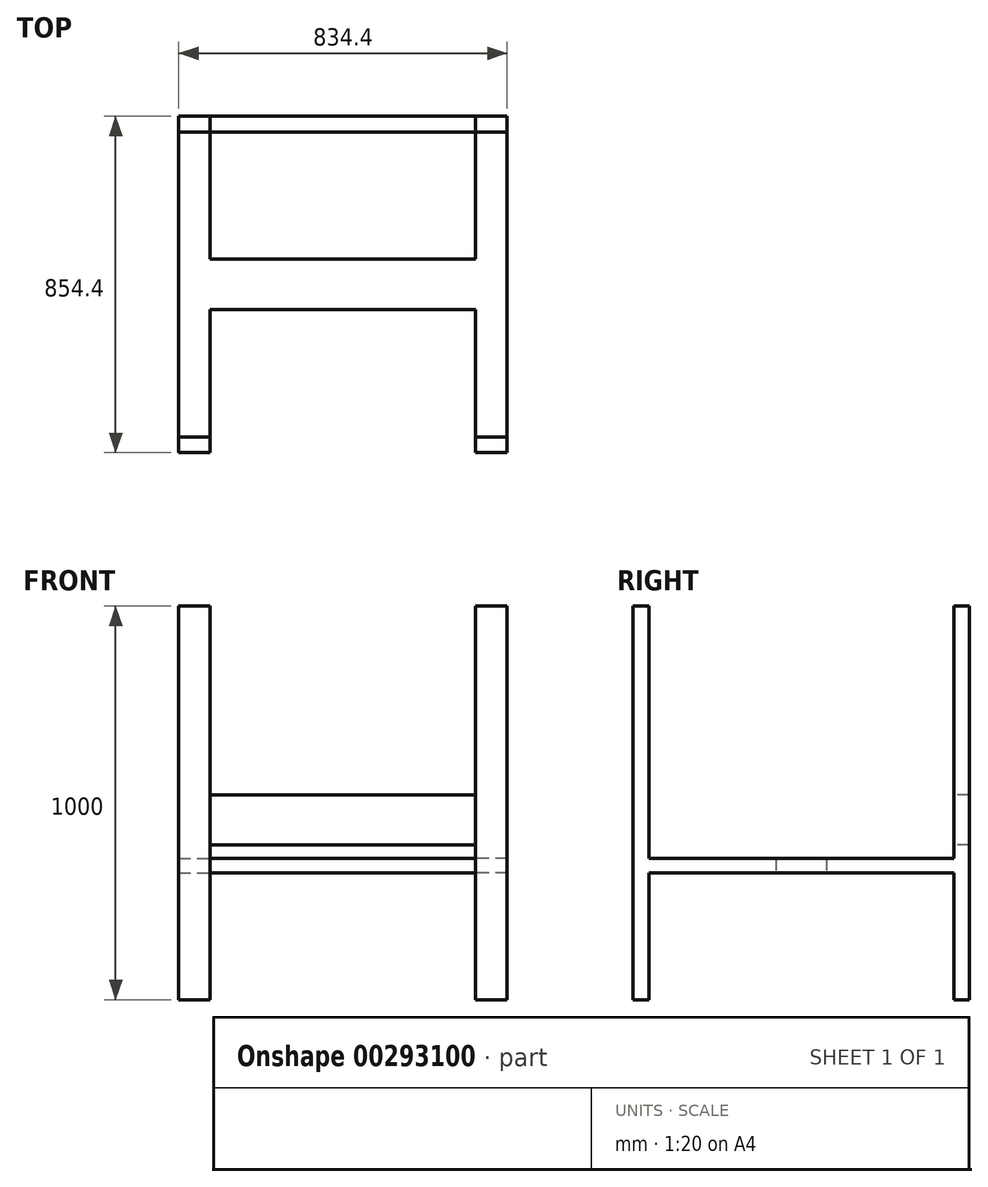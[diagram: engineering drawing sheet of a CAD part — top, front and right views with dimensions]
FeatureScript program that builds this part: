
annotation { "Feature Type Name" : "Feature", "Feature Type Description" : "" }
export const myFeature = defineFeature(function(context is Context, id is Id, definition is map)
    precondition{}
    {
        {
            var Q0;
            Q0=qCreatedBy(makeId("Top.planeOp"),FACE);
            var sketch = newSketch(context, id + "F0", { "sketchPlane" : qUnion([Q0])});
            skLineSegment(sketch, "E0.bottom", {"start": v(-457.2, 457.2) * mm, "end": v(457.2, 457.2) * mm});
            skLineSegment(sketch, "E0.top", {"start": v(-457.2, -457.2) * mm, "end": v(457.2, -457.2) * mm});
            skLineSegment(sketch, "E0.left", {"start": v(-457.2, 457.2) * mm, "end": v(-457.2, -457.2) * mm});
            skLineSegment(sketch, "E0.right", {"start": v(457.2, 457.2) * mm, "end": v(457.2, -457.2) * mm});
            skPoint(sketch, "E0.middle", {"position": v(0, 0) * mm});
            skLineSegment(sketch, "E1.bottom", {"start": v(-417.2, -427.2) * mm, "end": v(-337.2, -427.2) * mm});
            skLineSegment(sketch, "E1.top", {"start": v(-417.2, -387.2) * mm, "end": v(-337.2, -387.2) * mm});
            skLineSegment(sketch, "E1.left", {"start": v(-417.2, -427.2) * mm, "end": v(-417.2, -387.2) * mm});
            skLineSegment(sketch, "E1.right", {"start": v(-337.2, -427.2) * mm, "end": v(-337.2, -387.2) * mm});
            skLineSegment(sketch, "E2.MirrorCS", {"start": v(-417.2, 387.2) * mm, "end": v(-337.2, 387.2) * mm});
            skLineSegment(sketch, "E3.MirrorCS", {"start": v(-417.2, 427.2) * mm, "end": v(-337.2, 427.2) * mm});
            skLineSegment(sketch, "E4.MirrorCS", {"start": v(-337.2, 427.2) * mm, "end": v(-337.2, 387.2) * mm});
            skLineSegment(sketch, "E5.MirrorCS", {"start": v(-417.2, 427.2) * mm, "end": v(-417.2, 387.2) * mm});
            skLineSegment(sketch, "E6.MirrorCS", {"start": v(337.2, 427.2) * mm, "end": v(337.2, 387.2) * mm});
            skLineSegment(sketch, "E7.MirrorCS", {"start": v(417.2, 387.2) * mm, "end": v(337.2, 387.2) * mm});
            skLineSegment(sketch, "E8.MirrorCS", {"start": v(417.2, 427.2) * mm, "end": v(337.2, 427.2) * mm});
            skLineSegment(sketch, "E9.MirrorCS", {"start": v(417.2, 427.2) * mm, "end": v(417.2, 387.2) * mm});
            skLineSegment(sketch, "E10.MirrorCS", {"start": v(337.2, -427.2) * mm, "end": v(337.2, -387.2) * mm});
            skLineSegment(sketch, "E11.MirrorCS", {"start": v(417.2, -387.2) * mm, "end": v(337.2, -387.2) * mm});
            skLineSegment(sketch, "E12.MirrorCS", {"start": v(417.2, -427.2) * mm, "end": v(337.2, -427.2) * mm});
            skLineSegment(sketch, "E13.MirrorCS", {"start": v(417.2, -427.2) * mm, "end": v(417.2, -387.2) * mm});
            skSolve(sketch);
        }
        {
            var Q0;
            Q0=makeQuery(id+"F0.imprint","IMPRINT",FACE,{"disambiguationData":[TD([[makeQuery(id+"F0.imprint","IMPRINT",EDGE,{"derivedFrom":sQuery(id+"F0.wireOp",EDGE,"E0.bottom")}),-1.0]])]});
            var Q1;
            Q1=makeQuery(id+"F0.imprint","IMPRINT",FACE,{"disambiguationData":[TD([[makeQuery(id+"F0.imprint","IMPRINT",EDGE,{"derivedFrom":sQuery(id+"F0.wireOp",EDGE,"E1.bottom")}),1.0]])]});
            var Q2;
            Q2=makeQuery(id+"F0.imprint","IMPRINT",FACE,{"disambiguationData":[TD([[makeQuery(id+"F0.imprint","IMPRINT",EDGE,{"derivedFrom":sQuery(id+"F0.wireOp",EDGE,"E6.MirrorCS")}),1.0]])]});
            var Q3;
            Q3=makeQuery(id+"F0.imprint","IMPRINT",FACE,{"disambiguationData":[TD([[makeQuery(id+"F0.imprint","IMPRINT",EDGE,{"derivedFrom":sQuery(id+"F0.wireOp",EDGE,"E10.MirrorCS")}),-1.0]])]});
            var Q4;
            Q4=makeQuery(id+"F0.imprint","IMPRINT",FACE,{"disambiguationData":[TD([[makeQuery(id+"F0.imprint","IMPRINT",EDGE,{"derivedFrom":sQuery(id+"F0.wireOp",EDGE,"E2.MirrorCS")}),1.0]])]});
            var Q5;
            Q5=makeQuery(id+"F0.imprint","IMPRINT",FACE,{"disambiguationData":[TD([[makeQuery(id+"F0.imprint","IMPRINT",EDGE,{"derivedFrom":sQuery(id+"F0.wireOp",EDGE,"8inZ48Au-BpXX-FDBc-ttF8-S0e7Y6VRDIfR.bottom")}),-1.0]])]});
            extrude(context, id + "F1", {"entities" : qUnion([Q0, Q1, Q2, Q3, Q4, Q5]), "depth" : 40 * mm});
        }
        {
            var Q0;
            Q0=makeQuery(id+"F0.imprint","IMPRINT",FACE,{"disambiguationData":[TD([[makeQuery(id+"F0.imprint","IMPRINT",EDGE,{"derivedFrom":sQuery(id+"F0.wireOp",EDGE,"E1.bottom")}),1.0]])]});
            var Q1;
            Q1=makeQuery(id+"F0.imprint","IMPRINT",FACE,{"disambiguationData":[TD([[makeQuery(id+"F0.imprint","IMPRINT",EDGE,{"derivedFrom":sQuery(id+"F0.wireOp",EDGE,"E2.MirrorCS")}),1.0]])]});
            var Q2;
            Q2=makeQuery(id+"F0.imprint","IMPRINT",FACE,{"disambiguationData":[TD([[makeQuery(id+"F0.imprint","IMPRINT",EDGE,{"derivedFrom":sQuery(id+"F0.wireOp",EDGE,"E10.MirrorCS")}),-1.0]])]});
            var Q3;
            Q3=makeQuery(id+"F0.imprint","IMPRINT",FACE,{"disambiguationData":[TD([[makeQuery(id+"F0.imprint","IMPRINT",EDGE,{"derivedFrom":sQuery(id+"F0.wireOp",EDGE,"E6.MirrorCS")}),1.0]])]});
            extrude(context, id + "F2", {"entities" : qUnion([Q0, Q1, Q2, Q3]), "operationType" : NewBodyOperationType.ADD, "oppositeDirection" : true, "depth" : 1000 * mm});
        }
        {
            var Q0;
            Q0=makeQuery(id+"F0.imprint","IMPRINT",FACE,{"disambiguationData":[TD([[makeQuery(id+"F0.imprint","IMPRINT",EDGE,{"derivedFrom":sQuery(id+"F0.wireOp",EDGE,"E0.bottom")}),-1.0]])]});
            cPlane(context, id + "F3", {"entities" : qUnion([Q0]), "cplaneType" : CPlaneType.OFFSET, "offset" : 607 * mm, "oppositeDirection" : true, "width" : 150 * mm, "height" : 150 * mm});
        }
        {
            var Q0;
            Q0=qCreatedBy(id+"F3.planeOp",FACE);
            var sketch = newSketch(context, id + "F4", { "sketchPlane" : qUnion([Q0])});
            skLineSegment(sketch, "E14.bottom", {"start": v(-337.2, 427.2) * mm, "end": v(337.2, 427.2) * mm});
            skLineSegment(sketch, "E14.top", {"start": v(-337.2, 387.2) * mm, "end": v(337.2, 387.2) * mm});
            skLineSegment(sketch, "E14.left", {"start": v(-337.2, 427.2) * mm, "end": v(-337.2, 387.2) * mm});
            skLineSegment(sketch, "E14.right", {"start": v(337.2, 427.2) * mm, "end": v(337.2, 387.2) * mm});
            skSolve(sketch);
        }
        {
            var Q0;
            Q0=makeQuery(id+"F4.imprint","IMPRINT",FACE,{"disambiguationData":[TD([[makeQuery(id+"F4.imprint","IMPRINT",EDGE,{"derivedFrom":sQuery(id+"F4.wireOp",EDGE,"E14.bottom")}),-1.0]])]});
            extrude(context, id + "F5", {"entities" : qUnion([Q0]), "operationType" : NewBodyOperationType.ADD, "depth" : 127 * mm});
        }
        {
            var Q0;
            Q0=makeQuery(id+"F0.imprint","IMPRINT",FACE,{"disambiguationData":[TD([[makeQuery(id+"F0.imprint","IMPRINT",EDGE,{"derivedFrom":sQuery(id+"F0.wireOp",EDGE,"E0.bottom")}),-1.0]])]});
            cPlane(context, id + "F6", {"entities" : qUnion([Q0]), "cplaneType" : CPlaneType.OFFSET, "offset" : 678 * mm, "oppositeDirection" : true, "width" : 150 * mm, "height" : 150 * mm});
        }
        {
            var Q0;
            Q0=qCreatedBy(id+"F6.planeOp",FACE);
            var sketch = newSketch(context, id + "F7", { "sketchPlane" : qUnion([Q0])});
            skLineSegment(sketch, "E15.bottom", {"start": v(-417.2, -387.2) * mm, "end": v(-337.2, -387.2) * mm});
            skLineSegment(sketch, "E15.top", {"start": v(-417.2, 387.2) * mm, "end": v(-337.2, 387.2) * mm});
            skLineSegment(sketch, "E15.left", {"start": v(-417.2, -387.2) * mm, "end": v(-417.2, 387.2) * mm});
            skLineSegment(sketch, "E15.right", {"start": v(-337.2, -387.2) * mm, "end": v(-337.2, 387.2) * mm});
            skLineSegment(sketch, "E16.MirrorCS", {"start": v(417.2, -387.2) * mm, "end": v(417.2, 387.2) * mm});
            skLineSegment(sketch, "E17.MirrorCS", {"start": v(337.2, -387.2) * mm, "end": v(337.2, 387.2) * mm});
            skLineSegment(sketch, "E18.MirrorCS", {"start": v(417.2, -387.2) * mm, "end": v(337.2, -387.2) * mm});
            skLineSegment(sketch, "E19.MirrorCS", {"start": v(417.2, 387.2) * mm, "end": v(337.2, 387.2) * mm});
            skLineSegment(sketch, "E20.bottom", {"start": v(-337.2, -64) * mm, "end": v(337.2, -64) * mm});
            skLineSegment(sketch, "E20.top", {"start": v(-337.2, 64) * mm, "end": v(337.2, 64) * mm});
            skLineSegment(sketch, "E20.left", {"start": v(-337.2, -64) * mm, "end": v(-337.2, 64) * mm});
            skLineSegment(sketch, "E20.right", {"start": v(337.2, -64) * mm, "end": v(337.2, 64) * mm});
            skPoint(sketch, "E20.middle", {"position": v(0, 0) * mm});
            skSolve(sketch);
        }
        {
            var Q0;
            {var subQ1=sQuery(id+"F7.wireOp",EDGE,"E15.bottom");Q0=makeQuery(id+"F7.imprint","IMPRINT",FACE,{"disambiguationData":[TD([[makeQuery(id+"F7.imprint","IMPRINT",EDGE,{"derivedFrom":subQ1}),1.0]])]});}
            var Q1;
            Q1=makeQuery(id+"F7.imprint","IMPRINT",FACE,{"disambiguationData":[TD([[makeQuery(id+"F7.imprint","IMPRINT",EDGE,{"derivedFrom":sQuery(id+"F7.wireOp",EDGE,"E16.MirrorCS")}),1.0]])]});
            var Q2;
            Q2=makeQuery(id+"F7.imprint","IMPRINT",FACE,{"disambiguationData":[TD([[makeQuery(id+"F7.imprint","IMPRINT",EDGE,{"derivedFrom":sQuery(id+"F7.wireOp",EDGE,"E20.bottom")}),1.0]])]});
            extrude(context, id + "F8", {"entities" : qUnion([Q0, Q1, Q2]), "operationType" : NewBodyOperationType.ADD, "depth" : 37 * mm});
        }
        {
            var Q0;
            Q0=makeQuery(id+"F1.opExtrude","CAP_FACE",FACE,{"disambiguationData":[OSD([sQuery(id+"F0.wireOp",EDGE,"E0.bottom"),sQuery(id+"F0.wireOp",EDGE,"E0.top"),sQuery(id+"F0.wireOp",EDGE,"E0.left"),sQuery(id+"F0.wireOp",EDGE,"E0.right")])],"isStart":false});
            extrude(context, id + "F9", {"entities" : qUnion([Q0]), "operationType" : NewBodyOperationType.REMOVE, "oppositeDirection" : true, "depth" : 40 * mm});
        }
    });
